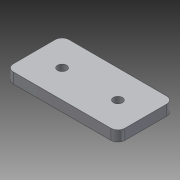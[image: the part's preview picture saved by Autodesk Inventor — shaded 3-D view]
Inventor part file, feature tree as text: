
AUTODESK INVENTOR PART (.ipt)
format: ipt  version: 2014 SP1 (Build 180222100, 222)  size: 97,792 bytes
history: native  units: in
note: dims shown in document units (in); Inventor stores cm internally (conversion verified against a paired STEP export)
features: extrude x2, sketch x2
ambient origin geometry x8: Origin, YZ Plane, XZ Plane, XY Plane, X Axis, Y Axis, Z Axis, Center Point
bodies: Solid1 (feature_tree)
feature tree (4):
  extrude  "Extrusion1"  Depth=2.0in
  extrude  "Extrusion2"  Depth=0.1875in TaperAngle=0.0deg
  sketch  "Sketch1"  dims[d0=1.0in d1=2.0in]
  sketch  "Sketch2"  dims[d2=0.125in d3=0.1875in d4=0.0in d5=0.164in d6=0.5in d7=0.5in d8=0.7874in d10=1.0in d11=0.3937in d13=1.0in d15=0.1875in d16=0.0in]
